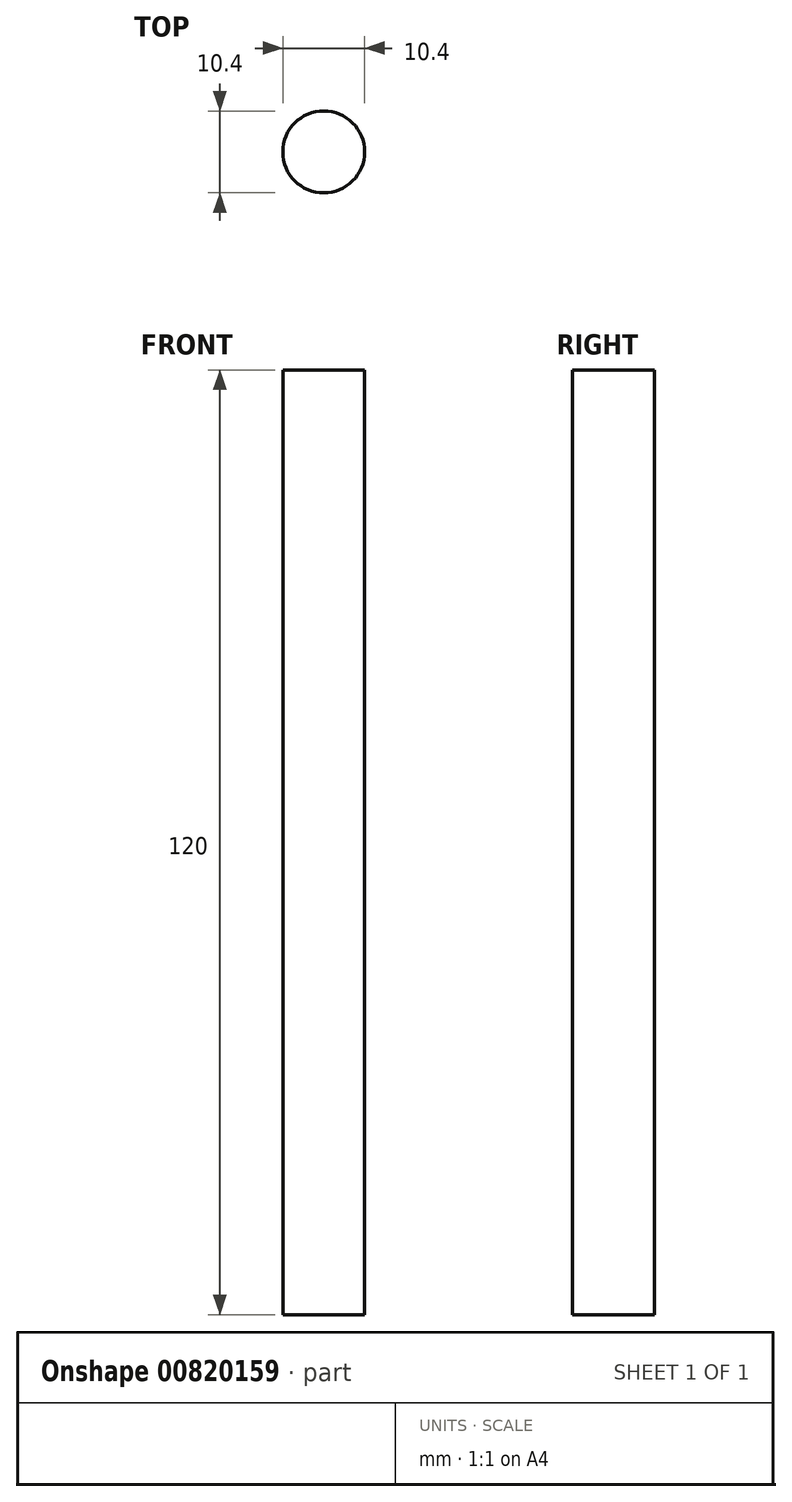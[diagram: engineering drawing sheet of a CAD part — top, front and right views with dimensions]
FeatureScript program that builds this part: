
annotation { "Feature Type Name" : "Feature", "Feature Type Description" : "" }
export const myFeature = defineFeature(function(context is Context, id is Id, definition is map)
    precondition{}
    {
        {
            var Q0;
            Q0=qCreatedBy(makeId("Top.planeOp"),FACE);
            var sketch = newSketch(context, id + "F0", { "sketchPlane" : qUnion([Q0])});
            skCircle(sketch, "E0", {"center": v(0, 0) * mm, "radius": 5.2 * mm});
            skSolve(sketch);
        }
        {
            var Q0;
            Q0 = qSketchRegion(id + "F0", true);
            extrude(context, id + "F1", {"entities" : qUnion([Q0]), "depth" : 120 * mm, "offsetDistance" : 25 * mm});
        }
    });
